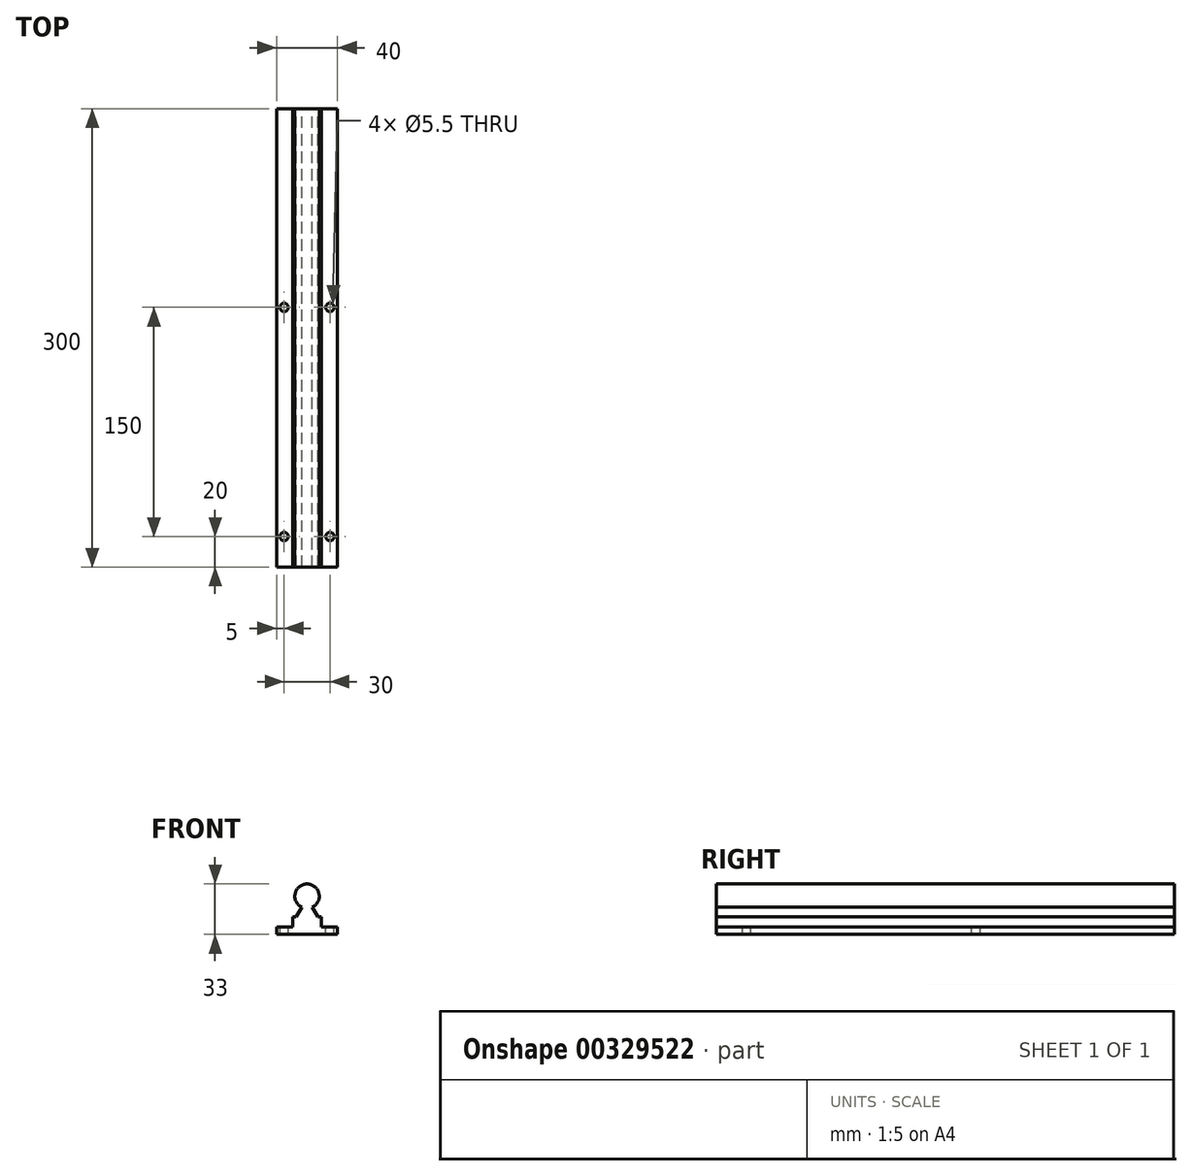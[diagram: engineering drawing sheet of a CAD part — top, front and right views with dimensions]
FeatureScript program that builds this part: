
annotation { "Feature Type Name" : "Feature", "Feature Type Description" : "" }
export const myFeature = defineFeature(function(context is Context, id is Id, definition is map)
    precondition{}
    {
        {
            var Q0;
            Q0=qCreatedBy(makeId("Front.planeOp"),FACE);
            var sketch = newSketch(context, id + "F0", { "sketchPlane" : qUnion([Q0])});
            skCircle(sketch, "E0", {"center": v(0, 0) * mm, "radius": 8 * mm});
            skLineSegment(sketch, "E1", {"start": v(-3.49, -7.2) * mm, "end": v(-7, -13.3) * mm});
            skLineSegment(sketch, "E2", {"start": v(-9.25, -13.3) * mm, "end": v(-9.25, -20) * mm});
            skLineSegment(sketch, "E3", {"start": v(-9.25, -20) * mm, "end": v(-20, -20) * mm});
            skLineSegment(sketch, "E4", {"start": v(-20, -20) * mm, "end": v(-20, -25) * mm});
            skLineSegment(sketch, "E5", {"start": v(-20, -25) * mm, "end": v(20, -25) * mm});
            skLineSegment(sketch, "E6", {"start": v(20, -25) * mm, "end": v(20, -20) * mm});
            skLineSegment(sketch, "E7", {"start": v(20, -20) * mm, "end": v(9.25, -20) * mm});
            skLineSegment(sketch, "E8", {"start": v(9.25, -20) * mm, "end": v(9.25, -13.3) * mm});
            skLineSegment(sketch, "E9", {"start": v(7, -13.3) * mm, "end": v(3.49, -7.2) * mm});
            skPoint(sketch, "E10", {"position": v(0, -25) * mm});
            skLineSegment(sketch, "E11", {"start": v(-9.25, -13.3) * mm, "end": v(-7, -13.3) * mm});
            skLineSegment(sketch, "E12", {"start": v(7, -13.3) * mm, "end": v(9.25, -13.3) * mm});
            skSolve(sketch);
        }
        {
            var Q0;
            Q0=qSketchRegion(id+"F0",true);
            extrude(context, id + "F1", {"entities" : qUnion([Q0]), "endBound" : BoundingType.SYMMETRIC, "depth" : 300 * mm});
        }
        {
            var Q0;
            Q0=makeQuery(id+"F1.opExtrude","SWEPT_FACE",FACE,{"disambiguationData":[OSD([sQuery(id+"F0.wireOp",EDGE,"E7")])]});
            var sketch = newSketch(context, id + "F2", { "sketchPlane" : qUnion([Q0])});
            skCircle(sketch, "E13", {"center": v(-15, -130) * mm, "radius": 2.75 * mm});
            skCircle(sketch, "E14", {"center": v(15, -130) * mm, "radius": 2.75 * mm});
            skCircle(sketch, "E15.0.1.0", {"center": v(-15, 20) * mm, "radius": 2.75 * mm});
            skCircle(sketch, "E15.0.1.1", {"center": v(15, 20) * mm, "radius": 2.75 * mm});
            skCircle(sketch, "E15.0.2.0", {"center": v(-15, 170) * mm, "radius": 2.75 * mm});
            skCircle(sketch, "E15.0.2.1", {"center": v(15, 170) * mm, "radius": 2.75 * mm});
            skCircle(sketch, "E15.0.3.0", {"center": v(-15, 320) * mm, "radius": 2.75 * mm});
            skCircle(sketch, "E15.0.3.1", {"center": v(15, 320) * mm, "radius": 2.75 * mm});
            skCircle(sketch, "E15.0.4.0", {"center": v(-15, 470) * mm, "radius": 2.75 * mm});
            skCircle(sketch, "E15.0.4.1", {"center": v(15, 470) * mm, "radius": 2.75 * mm});
            skCircle(sketch, "E15.0.5.0", {"center": v(-15, 620) * mm, "radius": 2.75 * mm});
            skCircle(sketch, "E15.0.5.1", {"center": v(15, 620) * mm, "radius": 2.75 * mm});
            skCircle(sketch, "E15.0.6.0", {"center": v(-15, 770) * mm, "radius": 2.75 * mm});
            skCircle(sketch, "E15.0.6.1", {"center": v(15, 770) * mm, "radius": 2.75 * mm});
            skCircle(sketch, "E15.0.7.0", {"center": v(-15, 920) * mm, "radius": 2.75 * mm});
            skCircle(sketch, "E15.0.7.1", {"center": v(15, 920) * mm, "radius": 2.75 * mm});
            skCircle(sketch, "E15.0.8.0", {"center": v(-15, 1070) * mm, "radius": 2.75 * mm});
            skCircle(sketch, "E15.0.8.1", {"center": v(15, 1070) * mm, "radius": 2.75 * mm});
            skLineSegment(sketch, "E15.direction1", {"start": v(-15, -130) * mm, "end": v(-40, -130) * mm, "construction": true});
            skLineSegment(sketch, "E15.direction2", {"start": v(-15, -130) * mm, "end": v(-15, 20) * mm, "construction": true});
            skSolve(sketch);
        }
        {
            var Q0;
            Q0=qSketchRegion(id+"F2",true);
            extrude(context, id + "F3", {"entities" : qUnion([Q0]), "operationType" : NewBodyOperationType.REMOVE, "endBound" : BoundingType.THROUGH_ALL, "oppositeDirection" : true, "depth" : 25 * mm});
        }
    });
